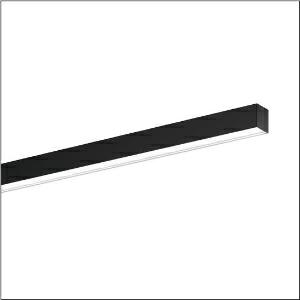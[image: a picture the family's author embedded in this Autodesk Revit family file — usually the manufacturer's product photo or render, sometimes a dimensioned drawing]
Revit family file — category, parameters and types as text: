
# Revit family: silica_r__21_51mx23da34bb_8ce5
name_source: partatom
category: Lighting Fixtures
units: mm (PartAtom-declared; Revit-internal decimal feet)

## family parameters
Cut with Voids When Loaded = No
Host = Face
Light Source = No
Part Type = Normal
Room Calculation Point = No
Round Connector Dimension = Use Diameter
Shared = No

## types (1)
- --- (1 x LED, 3280 lm, 24.1 W, 3000K)
    Apparent Load = 24 VA
    CIE Flux Codes = 78 96 99 100 100
    Color Rendering = 80
    Color Temperature = 3000K
    Default Elevation = 1800 mm
    Description = Silica® 21, office luminaire, primary optical cover: prismatic diffuser, of PMMA, CAT 2 (L<= 3000cd/m²), light emission: direct distribution, primary light characteristic: symmetric, installation type: surface-mounted, LED, rated luminous flux: 3.280lm, luminous efficacy: 136lm/W, light colour: 830, colour temperature: 3000K, with terminal, 3+2-pole, max. 2.5mm², mains connection: 220..240V, AC, 50/60Hz, rated input power: 24.1W, luminaire housing, of aluminium, jet black (RAL 9005), length: 1.204mm, width: 53mm, height: 53mm, protection rating (complete): IP20, insulation class (complete): insulation class I (protective earthing), certification: CE, permissible operating ambient temperature: 0..+35°C, standard: EN 50419, packaging unit: 1 piece
    Height = 0 mm  [stored 0 ft]
    Lamp = 1 x LED
    Lamp Light Flux = 3280 lm
    Lamp Power = 24.1 W
    Lamp count = 1
    Length = 1204 mm
    Luminous efficacy = 136 lm/W
    Manufacturer = Siteco
    ModVariant = No
    Model = 51MX23DA34BB
    Mounting Place = Ceiling
    Mounting Type = Recessed
    Number of Poles = 1
    OnlyDefault = Yes
    Power Factor = 1
    Product Name = Silica® 21
    Product group = office luminaire | ceiling recessed
    ProductGroupID = 400
    Protection Class = Protection class I
    Protection Degree = IP 20
    RLX_Detail_Level = 1
    RLX_Emergency_Light_Flux = 0 lm
    RLX_Emergency_Type = 0
    RLX_Emergency_Type_DB = No
    RlxData = <blob elided: 23673 chars, md5=76b5279b>
    Socket = socket
    Standby Power = 0 W
    System Light Flux = 3280 lm
    System Power = 24 W
    Type Comments = factory setting: luminous flux: 100 % | dim-lin: 254 | 345 mA
    Type Image = l_1335925.jpg
    URL = http://relux.com
    VarID = @adj_088799
    Voltage = 0 V
    Weight = 0.00 kg
    Width = 53 mm

note: [stored X ft] marks values corroborated as IEEE doubles in the binary element streams (Revit-internal decimal feet)

## geometry (parser evidence)
native form markers: Blend x4, Sweep x10
no freeform markers — native parametric forms only
